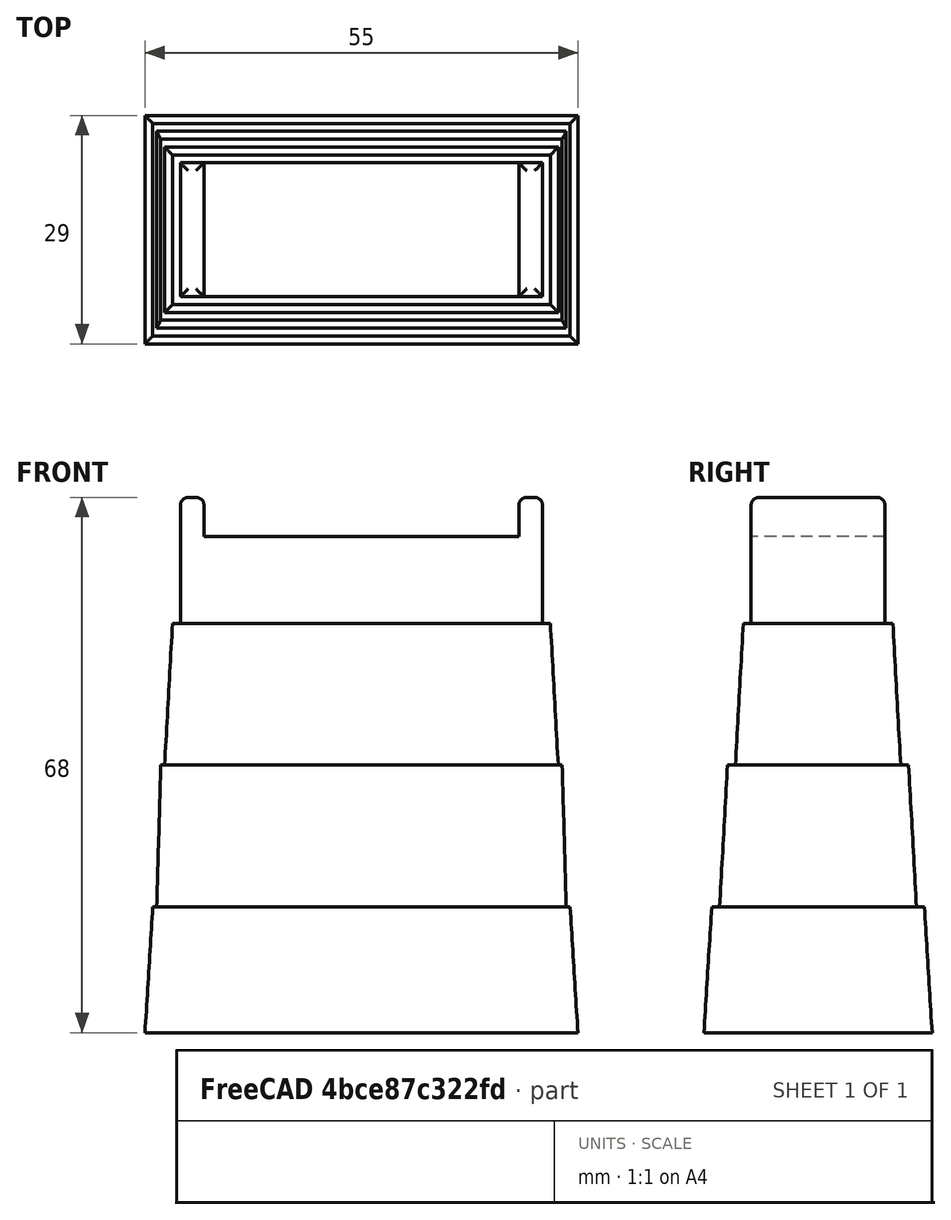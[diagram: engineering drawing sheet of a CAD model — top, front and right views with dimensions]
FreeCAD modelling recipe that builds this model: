
FCSTD DOCUMENT  (FreeCAD 0.18R4 (GitTag))
Label: Brio Pylon
License: All rights reserved
LicenseURL: http://en.wikipedia.org/wiki/All_rights_reserved
objects: TechDraw::DrawViewDimension×17, Sketcher::SketchObject×8, PartDesign::AdditiveLoft×3, TechDraw::DrawProjGroupItem×3, PartDesign::Pad×2, PartDesign::Mirrored×1, PartDesign::Fillet×1, PartDesign::Body×1, TechDraw::DrawSVGTemplate×1, TechDraw::DrawProjGroup×1, TechDraw::DrawViewPart×1, TechDraw::DrawPage×1, Mesh::Feature×1
note: 21 computed .brp shape members not serialized (recipe doc carries the construction recipe); baked Part::Feature solids carry a one-line shape summary decoded from their .brp

FEATURE [Sketcher::SketchObject] Sketch
  MapMode = 5
  Support = -> [XY_Plane]
  sketch-geometry (4):
    g0: LineSegment StartX=-27.5 StartY=14.5 StartZ=0 EndX=27.5 EndY=14.5 EndZ=0
    g1: LineSegment StartX=27.5 StartY=14.5 StartZ=0 EndX=27.5 EndY=-14.5 EndZ=0
    g2: LineSegment StartX=27.5 StartY=-14.5 StartZ=0 EndX=-27.5 EndY=-14.5 EndZ=0
    g3: LineSegment StartX=-27.5 StartY=-14.5 StartZ=0 EndX=-27.5 EndY=14.5 EndZ=0
  constraints (11):
    c: Coincident(g0,g1)
    c: Coincident(g1,g2)
    c: Coincident(g2,g3)
    c: Coincident(g3,g0)
    c: Horizontal(g0)
    c: Horizontal(g2)
    c: Vertical(g1)
    c: Vertical(g3)
    c: DistanceX(g0,g0) = 55
    c: DistanceY(g1,g1) = 29
    c: Symmetric(g0,g1,g-1)
FEATURE [Sketcher::SketchObject] Sketch001
  ExternalGeometry = -> [Sketch]
  MapMode = 5
  Placement = pos=(0,0,16) rot=(0,0,1;0rad)
  sketch-geometry (4):
    g0: LineSegment StartX=-26.5 StartY=13.5 StartZ=0 EndX=26.5 EndY=13.5 EndZ=0
    g1: LineSegment StartX=26.5 StartY=13.5 StartZ=0 EndX=26.5 EndY=-13.5 EndZ=0
    g2: LineSegment StartX=26.5 StartY=-13.5 StartZ=0 EndX=-26.5 EndY=-13.5 EndZ=0
    g3: LineSegment StartX=-26.5 StartY=-13.5 StartZ=0 EndX=-26.5 EndY=13.5 EndZ=0
  constraints (11):
    c: Coincident(g0,g1)
    c: Coincident(g1,g2)
    c: Coincident(g2,g3)
    c: Coincident(g3,g0)
    c: Horizontal(g0)
    c: Horizontal(g2)
    c: Vertical(g1)
    c: Vertical(g3)
    c: Symmetric(g0,g1,g-1)
    c: DistanceX(g0,g-4) = 1
    c: DistanceY(g0,g-4) = 1
FEATURE [PartDesign::AdditiveLoft] AdditiveLoft  label="1. Stock"
  Closed = true
  Profile = -> Sketch
  Ruled = true
  Sections = -> [Sketch,Sketch001]
FEATURE [Sketcher::SketchObject] Sketch003
  ExternalGeometry = -> [AdditiveLoft]
  MapMode = 5
  Placement = pos=(0,0,16) rot=(0,0,1;0rad)
  Support = -> [AdditiveLoft]
  sketch-geometry (4):
    g0: LineSegment StartX=-26 StartY=12.5 StartZ=0 EndX=26 EndY=12.5 EndZ=0
    g1: LineSegment StartX=26 StartY=12.5 StartZ=0 EndX=26 EndY=-12.5 EndZ=0
    g2: LineSegment StartX=26 StartY=-12.5 StartZ=0 EndX=-26 EndY=-12.5 EndZ=0
    g3: LineSegment StartX=-26 StartY=-12.5 StartZ=0 EndX=-26 EndY=12.5 EndZ=0
  constraints (11):
    c: Coincident(g0,g1)
    c: Coincident(g1,g2)
    c: Coincident(g2,g3)
    c: Coincident(g3,g0)
    c: Horizontal(g0)
    c: Horizontal(g2)
    c: Vertical(g1)
    c: Vertical(g3)
    c: DistanceX(g0,g-3) = 0.5
    c: DistanceY(g0,g-3) = 1
    c: Symmetric(g0,g1,g-1)
FEATURE [Sketcher::SketchObject] Sketch004
  ExternalGeometry = -> [Sketch003]
  MapMode = 5
  Placement = pos=(0,0,34) rot=(0,0,1;0rad)
  sketch-geometry (4):
    g0: LineSegment StartX=-25.5 StartY=11.5 StartZ=0 EndX=25.5 EndY=11.5 EndZ=0
    g1: LineSegment StartX=25.5 StartY=11.5 StartZ=0 EndX=25.5 EndY=-11.5 EndZ=0
    g2: LineSegment StartX=25.5 StartY=-11.5 StartZ=0 EndX=-25.5 EndY=-11.5 EndZ=0
    g3: LineSegment StartX=-25.5 StartY=-11.5 StartZ=0 EndX=-25.5 EndY=11.5 EndZ=0
  constraints (11):
    c: Coincident(g0,g1)
    c: Coincident(g1,g2)
    c: Coincident(g2,g3)
    c: Coincident(g3,g0)
    c: Horizontal(g0)
    c: Horizontal(g2)
    c: Vertical(g1)
    c: Vertical(g3)
    c: Symmetric(g0,g1,g-1)
    c: DistanceX(g0,g-3) = 0.5
    c: DistanceY(g0,g-3) = 1
FEATURE [PartDesign::AdditiveLoft] AdditiveLoft001  label="2. Stock"
  BaseFeature = -> AdditiveLoft
  Closed = false
  Profile = -> Sketch003
  Ruled = false
  Sections = -> [Sketch004]
FEATURE [Sketcher::SketchObject] Sketch005
  ExternalGeometry = -> [AdditiveLoft001]
  MapMode = 5
  Placement = pos=(0,0,34) rot=(0,0,1;0rad)
  Support = -> [AdditiveLoft001]
  sketch-geometry (4):
    g0: LineSegment StartX=25 StartY=10.5 StartZ=0 EndX=-25 EndY=10.5 EndZ=0
    g1: LineSegment StartX=-25 StartY=10.5 StartZ=0 EndX=-25 EndY=-10.5 EndZ=0
    g2: LineSegment StartX=-25 StartY=-10.5 StartZ=0 EndX=25 EndY=-10.5 EndZ=0
    g3: LineSegment StartX=25 StartY=-10.5 StartZ=0 EndX=25 EndY=10.5 EndZ=0
  constraints (11):
    c: Coincident(g0,g1)
    c: Coincident(g1,g2)
    c: Coincident(g2,g3)
    c: Coincident(g3,g0)
    c: Horizontal(g0)
    c: Horizontal(g2)
    c: Vertical(g1)
    c: Vertical(g3)
    c: Symmetric(g0,g1,g-1)
    c: DistanceY(g0,g-3) = 1
    c: DistanceX(g-3,g0) = 0.5
FEATURE [Sketcher::SketchObject] Sketch006
  ExternalGeometry = -> [Sketch005]
  MapMode = 5
  Placement = pos=(0,0,52) rot=(0,0,1;0rad)
  sketch-geometry (4):
    g0: LineSegment StartX=-24 StartY=9.5 StartZ=0 EndX=24 EndY=9.5 EndZ=0
    g1: LineSegment StartX=24 StartY=9.5 StartZ=0 EndX=24 EndY=-9.5 EndZ=0
    g2: LineSegment StartX=24 StartY=-9.5 StartZ=0 EndX=-24 EndY=-9.5 EndZ=0
    g3: LineSegment StartX=-24 StartY=-9.5 StartZ=0 EndX=-24 EndY=9.5 EndZ=0
  constraints (11):
    c: Coincident(g0,g1)
    c: Coincident(g1,g2)
    c: Coincident(g2,g3)
    c: Coincident(g3,g0)
    c: Horizontal(g0)
    c: Horizontal(g2)
    c: Vertical(g1)
    c: Vertical(g3)
    c: Symmetric(g0,g1,g-1)
    c: DistanceX(g0,g-3) = 1
    c: DistanceY(g0,g-3) = 1
FEATURE [PartDesign::AdditiveLoft] AdditiveLoft002  label="3. Stock"
  BaseFeature = -> AdditiveLoft001
  Closed = false
  Profile = -> Sketch005
  Ruled = false
  Sections = -> [Sketch006]
FEATURE [Sketcher::SketchObject] Sketch007
  ExternalGeometry = -> [AdditiveLoft002]
  MapMode = 5
  Placement = pos=(0,0,52) rot=(0,0,1;0rad)
  Support = -> [AdditiveLoft002]
  sketch-geometry (4):
    g0: LineSegment StartX=-23 StartY=8.5 StartZ=0 EndX=23 EndY=8.5 EndZ=0
    g1: LineSegment StartX=23 StartY=8.5 StartZ=0 EndX=23 EndY=-8.5 EndZ=0
    g2: LineSegment StartX=23 StartY=-8.5 StartZ=0 EndX=-23 EndY=-8.5 EndZ=0
    g3: LineSegment StartX=-23 StartY=-8.5 StartZ=0 EndX=-23 EndY=8.5 EndZ=0
  constraints (11):
    c: Coincident(g0,g1)
    c: Coincident(g1,g2)
    c: Coincident(g2,g3)
    c: Coincident(g3,g0)
    c: Horizontal(g0)
    c: Horizontal(g2)
    c: Vertical(g1)
    c: Vertical(g3)
    c: Symmetric(g0,g1,g-1)
    c: DistanceY(g0,g-3) = 1
    c: DistanceX(g0,g-3) = 1
FEATURE [PartDesign::Pad] Pad  label="4. Stock"
  BaseFeature = -> AdditiveLoft002
  Length = 11
  Length2 = 100
  Profile = -> Sketch007
  Type = 0
FEATURE [Sketcher::SketchObject] Sketch008  label="Schienenführung Form"
  ExternalGeometry = -> [Pad]
  MapMode = 5
  Placement = pos=(0,0,63) rot=(0,0,1;0rad)
  Support = -> [Pad]
  sketch-geometry (4):
    g0: LineSegment StartX=-23 StartY=8.5 StartZ=0 EndX=-20 EndY=8.5 EndZ=0
    g1: LineSegment StartX=-20 StartY=8.5 StartZ=0 EndX=-20 EndY=-8.5 EndZ=0
    g2: LineSegment StartX=-20 StartY=-8.5 StartZ=0 EndX=-23 EndY=-8.5 EndZ=0
    g3: LineSegment StartX=-23 StartY=-8.5 StartZ=0 EndX=-23 EndY=8.5 EndZ=0
  constraints (11):
    c: Coincident(g0,g1)
    c: Coincident(g1,g2)
    c: Coincident(g2,g3)
    c: Coincident(g3,g0)
    c: Horizontal(g0)
    c: Horizontal(g2)
    c: Vertical(g1)
    c: Vertical(g3)
    c: Coincident(g0,g-3)
    c: DistanceX(g0,g0) = 3
    c: DistanceY(g-4,g1) = 0
FEATURE [PartDesign::Pad] Pad001  label="Schienenführung"
  BaseFeature = -> Pad
  Length = 5
  Length2 = 100
  Profile = -> Sketch008
  Type = 0
FEATURE [PartDesign::Mirrored] Mirrored
  BaseFeature = -> Pad001
  MirrorPlane = -> Sketch008 [V_Axis]
  Originals = -> [Pad001]
FEATURE [PartDesign::Fillet] Fillet
  Base = -> Mirrored [Face35,Face33]
  BaseFeature = -> Mirrored
  Radius = 1
FEATURE [PartDesign::Body] Body  label="Pfeiler"
  Group = -> [Sketch,Sketch001,AdditiveLoft,Sketch003,Sketch004,AdditiveLoft001,Sketch005,Sketch006,AdditiveLoft002,Sketch007,Pad,Sketch008,Pad001,Mirrored,Fillet]
  Origin = -> Origin
  Tip = -> Fillet
FEATURE [TechDraw::DrawSVGTemplate] Template
  EditableTexts = Designed_by_Name=Onkel Marcel; Drawing_number=2; FC-Date=2021-02-07; FC-SC=1,5:1; FC-SH=1/1; FC-Title=Brio Brückenpfeiler; Subtitle=Projektmanager: Papa; Kunde: Leo; Weight=0,020 kg
  Height = 210
  Orientation = 1
  Width = 297
FEATURE [TechDraw::DrawProjGroupItem] ProjItem  label="Front"
  CoarseView = false
  Direction = (0,-1,0)
  Focus = 100
  HardHidden = false
  IsoCount = 0
  IsoHidden = false
  IsoVisible = false
  LockPosition = true
  Perspective = false
  Rotation = 0
  RotationVector = (1,0,0)
  Scale = 1.5
  ScaleType = 2
  SeamHidden = false
  SeamVisible = false
  SmoothHidden = false
  SmoothVisible = false
  Source = -> [Body]
  Type = 0
  X = 0
  Y = 0
FEATURE [TechDraw::DrawProjGroupItem] ProjItem001  label="Left"
  CoarseView = false
  Direction = (-1,-1e-16,0)
  Focus = 100
  HardHidden = false
  IsoCount = 0
  IsoHidden = false
  IsoVisible = false
  LockPosition = true
  Perspective = false
  Rotation = 0
  RotationVector = (1e-16,-1,0)
  Scale = 1.5
  ScaleType = 2
  SeamHidden = false
  SeamVisible = false
  SmoothHidden = false
  SmoothVisible = false
  Source = -> [Body]
  Type = 1
  X = 70.9023
  Y = 0
FEATURE [TechDraw::DrawProjGroupItem] ProjItem002  label="Top"
  CoarseView = false
  Direction = (0,0,1)
  Focus = 100
  HardHidden = false
  IsoCount = 0
  IsoHidden = false
  IsoVisible = false
  LockPosition = true
  Perspective = false
  Rotation = 0
  RotationVector = (1,0,0)
  Scale = 1.5
  ScaleType = 2
  SeamHidden = false
  SeamVisible = false
  SmoothHidden = false
  SmoothVisible = false
  Source = -> [Body]
  Type = 4
  X = 0
  Y = -94
FEATURE [TechDraw::DrawProjGroup] ProjGroup
  Anchor = -> ProjItem
  AutoDistribute = true
  LockPosition = false
  ProjectionType = 1
  Rotation = 0
  Scale = 1.5
  ScaleType = 2
  Source = -> [Body]
  Views = -> [ProjItem,ProjItem001,ProjItem002]
  X = 67.8759
  Y = 136.372
  spacingX = 15
  spacingY = 15
FEATURE [TechDraw::DrawViewDimension] Dimension
  Arbitrary = false
  FormatSpec = %.2f
  LockPosition = false
  MeasureType = 1
  OverTolerance = 0
  References2D = -> [ProjItem001]
  Rotation = 0
  ScaleType = 0
  Type = 2
  UnderTolerance = 0
  X = 37.6864
  Y = -1.18275
FEATURE [TechDraw::DrawViewDimension] Dimension001
  Arbitrary = false
  FormatSpec = %.2f
  LockPosition = false
  MeasureType = 1
  OverTolerance = 0
  References2D = -> [ProjItem001]
  Rotation = 0
  ScaleType = 0
  Type = 2
  UnderTolerance = 0
  X = 26.1638
  Y = -39.5914
FEATURE [TechDraw::DrawViewDimension] Dimension002
  Arbitrary = false
  FormatSpec = %.2f
  LockPosition = false
  MeasureType = 1
  OverTolerance = 0
  References2D = -> [ProjItem001]
  Rotation = 0
  ScaleType = 0
  Type = 1
  UnderTolerance = 0
  X = -1.47153
  Y = -63.8175
FEATURE [TechDraw::DrawViewDimension] Dimension003
  Arbitrary = false
  FormatSpec = %.2f
  LockPosition = false
  MeasureType = 1
  OverTolerance = 0
  References2D = -> [ProjItem001]
  Rotation = 0
  ScaleType = 0
  Type = 2
  UnderTolerance = 0
  X = 26.4471
  Y = -14.2358
FEATURE [TechDraw::DrawViewDimension] Dimension004
  Arbitrary = false
  FormatSpec = %.2f
  LockPosition = false
  MeasureType = 1
  OverTolerance = 0
  References2D = -> [ProjItem001]
  Rotation = 0
  ScaleType = 0
  Type = 2
  UnderTolerance = 0
  X = 26.3901
  Y = 13.5
FEATURE [TechDraw::DrawViewDimension] Dimension005
  Arbitrary = false
  FormatSpec = %.2f
  LockPosition = false
  MeasureType = 1
  OverTolerance = 0
  References2D = -> [ProjItem001]
  Rotation = 0
  ScaleType = 0
  Type = 2
  UnderTolerance = 0
  X = 18.888
  Y = 36.7215
FEATURE [TechDraw::DrawViewDimension] Dimension006
  Arbitrary = false
  FormatSpec = %.2f
  LockPosition = false
  MeasureType = 1
  OverTolerance = 0
  References2D = -> [ProjItem001]
  Rotation = 0
  ScaleType = 0
  Type = 2
  UnderTolerance = 0
  X = -30.5495
  Y = 51.9636
FEATURE [TechDraw::DrawViewDimension] Dimension007
  Arbitrary = false
  FormatSpec = %.2f
  LockPosition = false
  MeasureType = 1
  OverTolerance = 0
  References2D = -> [ProjItem]
  Rotation = 0
  ScaleType = 0
  Type = 1
  UnderTolerance = 0
  X = 0
  Y = -62.4044
FEATURE [TechDraw::DrawViewDimension] Dimension008
  Arbitrary = false
  FormatSpec = %.2f
  LockPosition = false
  MeasureType = 1
  OverTolerance = 0
  References2D = -> [ProjItem]
  Rotation = 0
  ScaleType = 0
  Type = 1
  UnderTolerance = 0
  X = 0
  Y = -29.6612
FEATURE [TechDraw::DrawViewDimension] Dimension010
  Arbitrary = false
  FormatSpec = %.2f
  LockPosition = false
  MeasureType = 1
  OverTolerance = 0
  References2D = -> [ProjItem]
  Rotation = 0
  ScaleType = 0
  Type = 1
  UnderTolerance = 0
  X = -0.96682
  Y = -2.66997
FEATURE [TechDraw::DrawViewDimension] Dimension011
  Arbitrary = false
  FormatSpec = %.2f
  LockPosition = false
  MeasureType = 1
  OverTolerance = 0
  References2D = -> [ProjItem]
  Rotation = 0
  ScaleType = 0
  Type = 1
  UnderTolerance = 0
  X = -0.821356
  Y = 7.3922
FEATURE [TechDraw::DrawViewDimension] Dimension013
  Arbitrary = false
  FormatSpec = %.2f
  LockPosition = false
  MeasureType = 1
  OverTolerance = 0
  References2D = -> [ProjItem]
  Rotation = 0
  ScaleType = 0
  Type = 1
  UnderTolerance = 0
  X = -0.205339
  Y = -19.2998
FEATURE [TechDraw::DrawViewDimension] Dimension014
  Arbitrary = false
  FormatSpec = %.2f
  LockPosition = false
  MeasureType = 1
  OverTolerance = 0
  References2D = -> [ProjItem]
  Rotation = 0
  ScaleType = 0
  Type = 1
  UnderTolerance = 0
  X = 18.2316
  Y = 41.1345
FEATURE [TechDraw::DrawViewDimension] Dimension015
  Arbitrary = false
  FormatSpec = %.2f
  LockPosition = false
  MeasureType = 1
  OverTolerance = 0
  References2D = -> [ProjItem]
  Rotation = 0
  ScaleType = 0
  Type = 1
  UnderTolerance = 0
  X = -18.1133
  Y = 40.8388
FEATURE [TechDraw::DrawViewPart] View
  CoarseView = false
  Direction = (-0.531,-0.838,0.127)
  Focus = 100
  HardHidden = false
  IsoCount = 0
  IsoHidden = false
  IsoVisible = false
  LockPosition = false
  Perspective = false
  Rotation = 0
  Scale = 1.5
  ScaleType = 0
  SeamHidden = false
  SeamVisible = false
  SmoothHidden = false
  SmoothVisible = true
  Source = -> [Body]
  X = 239.577
  Y = 134.822
FEATURE [TechDraw::DrawViewDimension] Dimension017
  Arbitrary = false
  FormatSpec = %.2f
  LockPosition = false
  MeasureType = 1
  OverTolerance = 0
  References2D = -> [ProjItem]
  Rotation = 0
  ScaleType = 0
  Type = 1
  UnderTolerance = 0
  X = -1.20899
  Y = 60.0228
FEATURE [TechDraw::DrawViewDimension] Dimension018
  Arbitrary = false
  FormatSpec = %.2f
  LockPosition = false
  MeasureType = 1
  OverTolerance = 0
  References2D = -> [ProjItem]
  Rotation = 0
  ScaleType = 0
  Type = 1
  UnderTolerance = 0
  X = 0.591376
  Y = 35.2793
FEATURE [TechDraw::DrawViewDimension] Dimension019
  Arbitrary = false
  FormatSpec = %.2f
  LockPosition = false
  MeasureType = 1
  OverTolerance = 0
  References2D = -> [ProjItem]
  Rotation = 0
  ScaleType = 0
  Type = 1
  UnderTolerance = 0
  X = -0.147844
  Y = 23.5996
FEATURE [TechDraw::DrawPage] Page  label="Technische Zeichnung Pfeiler"
  KeepUpdated = true
  ProjectionType = 0
  Template = -> Template
  Views = -> [ProjGroup,Dimension,Dimension001,Dimension002,Dimension003,Dimension004,Dimension005,Dimension006,Dimension007,Dimension008,Dimension010,Dimension011,Dimension013,Dimension014,Dimension015,View,Dimension017,Dimension018,Dimension019]
FEATURE [Mesh::Feature] Mesh  label="Brio_Pylon_Mesh"
